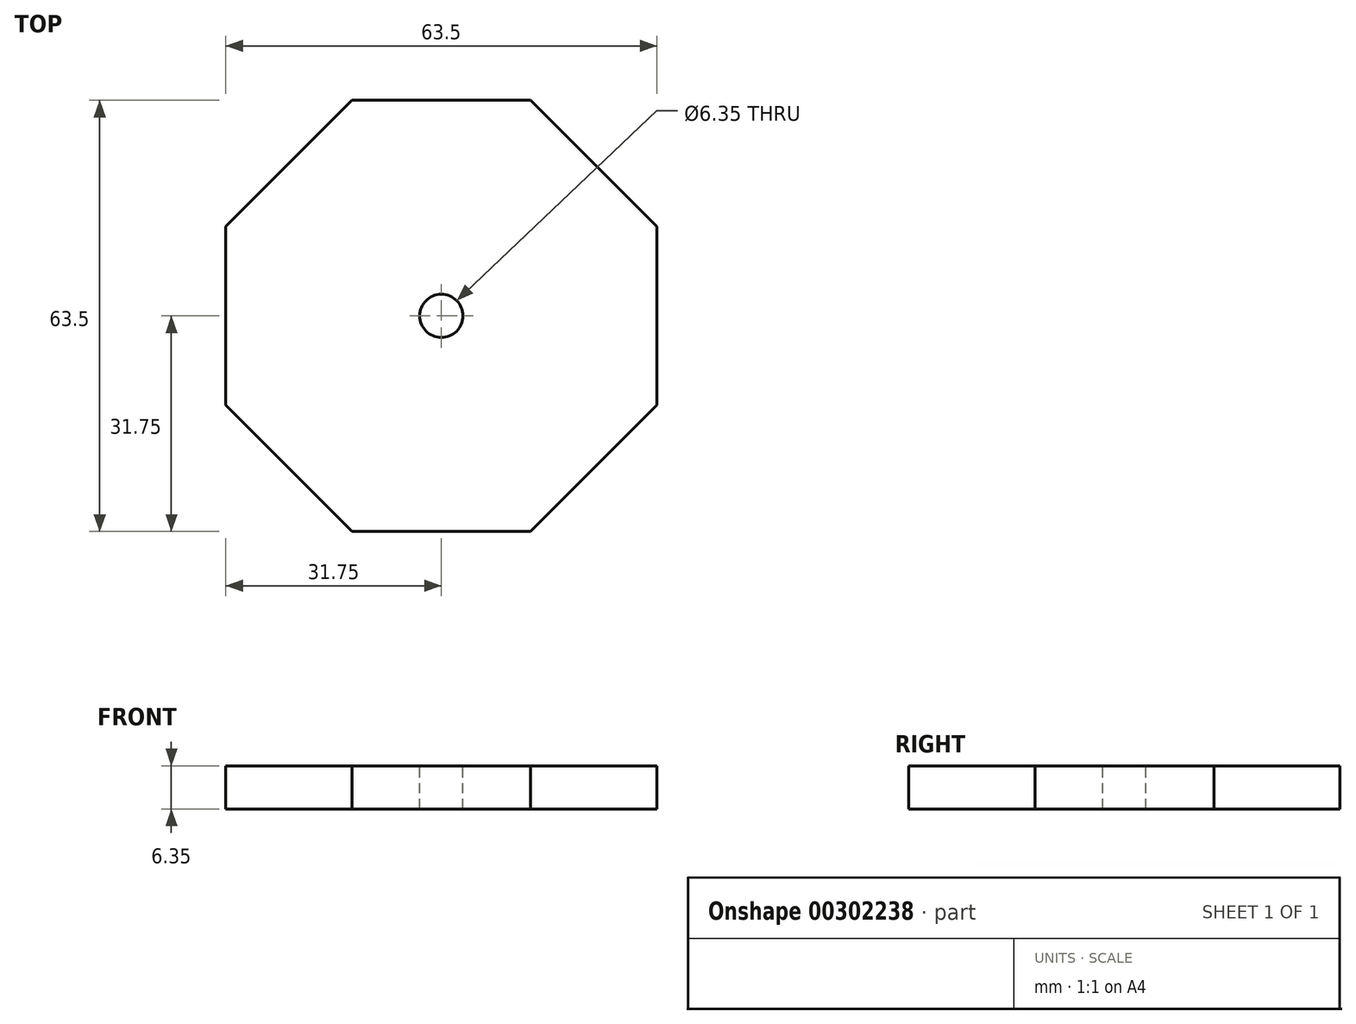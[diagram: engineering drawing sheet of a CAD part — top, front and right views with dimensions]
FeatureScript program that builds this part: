
annotation { "Feature Type Name" : "Feature", "Feature Type Description" : "" }
export const myFeature = defineFeature(function(context is Context, id is Id, definition is map)
    precondition{}
    {
        {
            var Q0;
            Q0=qCreatedBy(makeId("Top.planeOp"),FACE);
            var sketch = newSketch(context, id + "F0", { "sketchPlane" : qUnion([Q0])});
            skCircle(sketch, "E0.cCircle", {"center": v(0, 0) * mm, "radius": 31.75 * mm, "construction": true});
            skLineSegment(sketch, "E0.0", {"start": v(-31.75, -13.15) * mm, "end": v(-31.75, 13.15) * mm});
            skLineSegment(sketch, "E0.1", {"start": v(-31.75, 13.15) * mm, "end": v(-13.15, 31.75) * mm});
            skLineSegment(sketch, "E0.2", {"start": v(-13.15, 31.75) * mm, "end": v(13.15, 31.75) * mm});
            skLineSegment(sketch, "E0.3", {"start": v(13.15, 31.75) * mm, "end": v(31.75, 13.15) * mm});
            skLineSegment(sketch, "E0.4", {"start": v(31.75, 13.15) * mm, "end": v(31.75, -13.15) * mm});
            skLineSegment(sketch, "E0.5", {"start": v(31.75, -13.15) * mm, "end": v(13.15, -31.75) * mm});
            skLineSegment(sketch, "E0.6", {"start": v(13.15, -31.75) * mm, "end": v(-13.15, -31.75) * mm});
            skLineSegment(sketch, "E0.7", {"start": v(-13.15, -31.75) * mm, "end": v(-31.75, -13.15) * mm});
            skPoint(sketch, "E0.0.midPoint", {"position": v(-31.75, 0) * mm});
            skSolve(sketch);
        }
        {
            var Q0;
            Q0=makeQuery(id+"F0.imprint","IMPRINT",FACE,{"disambiguationData":[TD([[makeQuery(id+"F0.imprint","IMPRINT",EDGE,{"derivedFrom":sQuery(id+"F0.wireOp",EDGE,"E0.0")}),-1.0]])]});
            extrude(context, id + "F1", {"entities" : qUnion([Q0]), "depth" : 6.35 * mm, "hasDraft" : true, "draftAngle" : 0 * degree});
        }
        {
            var Q0;
            Q0=makeQuery(id+"F1.opExtrude","CAP_FACE",FACE,{"disambiguationData":[OSD([sQuery(id+"F0.wireOp",EDGE,"E0.0"),sQuery(id+"F0.wireOp",EDGE,"E0.1"),sQuery(id+"F0.wireOp",EDGE,"E0.2"),sQuery(id+"F0.wireOp",EDGE,"E0.3"),sQuery(id+"F0.wireOp",EDGE,"E0.4"),sQuery(id+"F0.wireOp",EDGE,"E0.5"),sQuery(id+"F0.wireOp",EDGE,"E0.6"),sQuery(id+"F0.wireOp",EDGE,"E0.7")])],"isStart":false});
            var sketch = newSketch(context, id + "F2", { "sketchPlane" : qUnion([Q0])});
            skCircle(sketch, "E1", {"center": v(0, 0) * mm, "radius": 3.18 * mm});
            skSolve(sketch);
        }
        {
            var Q0;
            Q0 = qSketchRegion(id + "F2", true);
            extrude(context, id + "F3", {"entities" : qUnion([Q0]), "operationType" : NewBodyOperationType.REMOVE, "oppositeDirection" : true, "depth" : 25.4 * mm});
        }
    });
